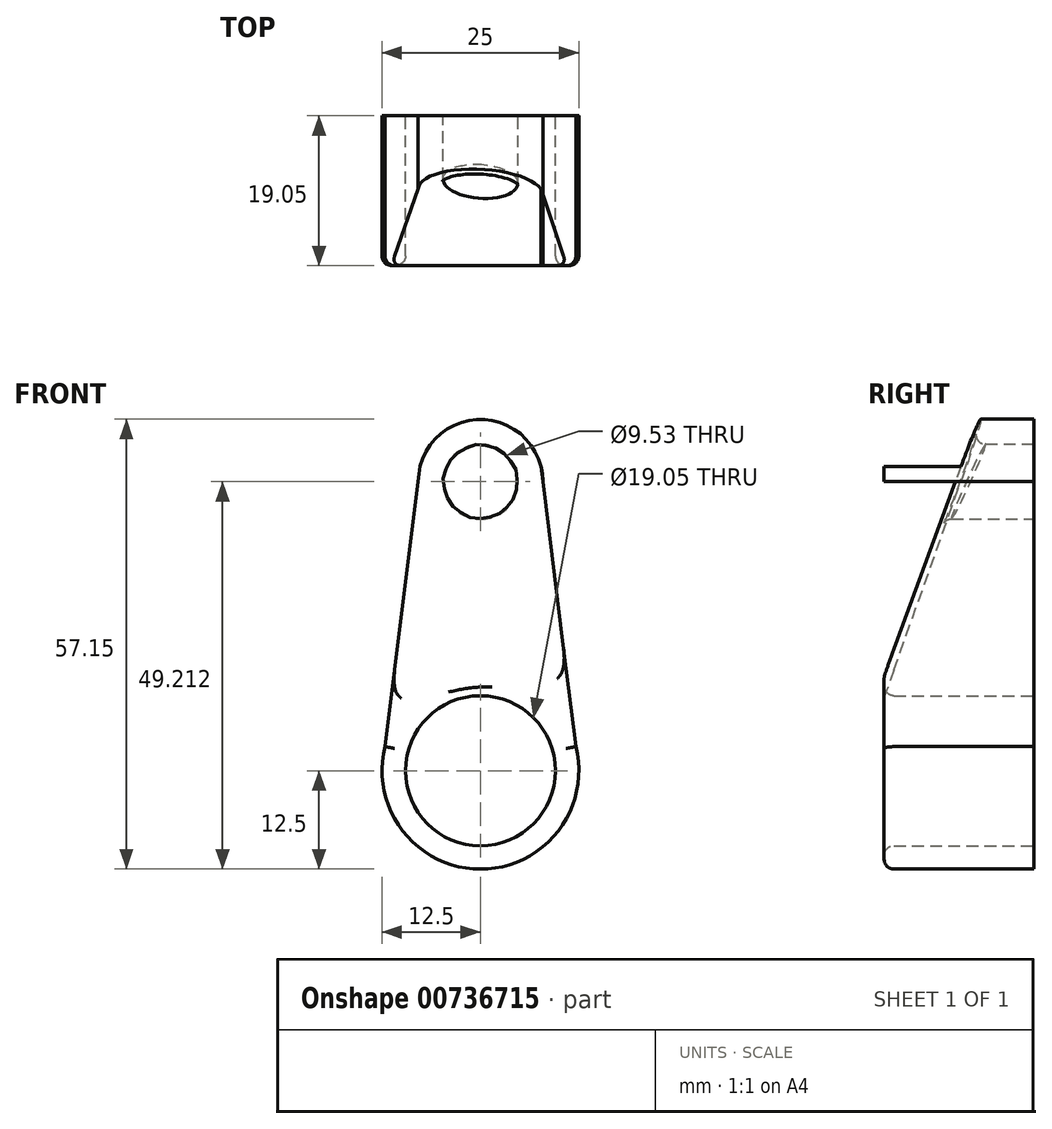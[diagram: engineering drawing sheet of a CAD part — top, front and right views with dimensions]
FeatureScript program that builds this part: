
annotation { "Feature Type Name" : "Feature", "Feature Type Description" : "" }
export const myFeature = defineFeature(function(context is Context, id is Id, definition is map)
    precondition{}
    {
        {
            var Q0;
            Q0=qCreatedBy(makeId("Front.planeOp"),FACE);
            var sketch = newSketch(context, id + "F0", { "sketchPlane" : qUnion([Q0])});
            skCircle(sketch, "E0", {"center": v(0, 0) * mm, "radius": 9.53 * mm});
            skCircle(sketch, "E1", {"center": v(0, 0) * mm, "radius": 12.5 * mm});
            skCircle(sketch, "E2", {"center": v(0, 36.71) * mm, "radius": 4.76 * mm});
            skCircle(sketch, "E3", {"center": v(0, 36.71) * mm, "radius": 7.94 * mm});
            skLineSegment(sketch, "E4", {"start": v(-12.5, 0) * mm, "end": v(-7.94, 36.71) * mm});
            skLineSegment(sketch, "E5", {"start": v(12.5, 0) * mm, "end": v(7.94, 36.71) * mm});
            skSolve(sketch);
        }
        {
            var Q0;
            Q0 = qSketchRegion(id + "F0", true);
            extrude(context, id + "F1", {"entities" : qUnion([Q0]), "depth" : 19.05 * mm, "offsetDistance" : 25 * mm});
        }
        {
            var Q0;
            Q0=makeQuery(id+"F1.opExtrude","SWEPT_FACE",FACE,{"disambiguationData":[OSD([sQuery(id+"F0.wireOp",EDGE,"E5")])]});
            var sketch = newSketch(context, id + "F2", { "sketchPlane" : qUnion([Q0])});
            skLineSegment(sketch, "E6", {"start": v(0, -1.87) * mm, "end": v(-19.05, -1.87) * mm, "construction": true});
            skLineSegment(sketch, "E7", {"start": v(-19.05, 10.63) * mm, "end": v(-19.05, 62.97) * mm});
            skLineSegment(sketch, "E8", {"start": v(-19.05, 62.97) * mm, "end": v(0, 62.97) * mm});
            skLineSegment(sketch, "E9", {"start": v(0, 62.97) * mm, "end": v(-19.05, 10.63) * mm});
            skSolve(sketch);
        }
        {
            var Q0;
            Q0 = qSketchRegion(id + "F2", true);
            extrude(context, id + "F3", {"entities" : qUnion([Q0]), "operationType" : NewBodyOperationType.REMOVE, "oppositeDirection" : true, "depth" : 25 * mm, "offsetDistance" : 25 * mm});
        }
        {
            var Q0;
            Q0=makeQuery(id+"F3.boolean.opBoolean","COPY",EDGE,{"derivedFrom":makeQuery(id+"F3.opExtrude","SWEPT_EDGE",EDGE,{"disambiguationData":[OSD([sQuery(id+"F0.wireOp",EDGE,"E5"),sQuery(id+"F2.wireOp",EDGE,"E7"),sQuery(id+"F2.wireOp",EDGE,"E9")])]})});
            var Q1;
            {var subQ0=sQuery(id+"F0.wireOp",EDGE,"E5");var subQ1=sQuery(id+"F0.wireOp",EDGE,"E4");var subQ2=sQuery(id+"F0.wireOp",EDGE,"E1");var subQ3=sQuery(id+"F0.wireOp",EDGE,"E0");Q1=makeQuery(id+"F3.boolean.opBoolean","SPLIT",FACE,{"disambiguationData":[TD([makeQuery(id+"F1.opExtrude","SWEPT_FACE",FACE,{"disambiguationData":[OSD([subQ3])]})])],"derivedFrom":makeQuery(id+"F1.opExtrude","CAP_FACE",FACE,{"disambiguationData":[OSD([subQ3,subQ2,sQuery(id+"F0.wireOp",EDGE,"E2"),sQuery(id+"F0.wireOp",EDGE,"E3"),subQ1,subQ0])],"isStart":false})});}
            fillet(context, id + "F4", {"entities" : qUnion([Q0, Q1]), "radius" : 1.25 * mm, "tangentPropagation" : true, "allowEdgeOverflow" : false});
        }
        {
            var Q0;
            Q0=makeQuery(id+"F3.boolean.opBoolean","INTERSECT",EDGE,{"derivedFrom":[makeQuery(id+"F1.opExtrude","SWEPT_FACE",FACE,{"disambiguationData":[OSD([sQuery(id+"F0.wireOp",EDGE,"E2")])]}),makeQuery(id+"F3.opExtrude","SWEPT_FACE",FACE,{"disambiguationData":[OSD([sQuery(id+"F2.wireOp",EDGE,"E9")])]})]});
            fillet(context, id + "F5", {"entities" : qUnion([Q0]), "radius" : 1.25 * mm, "tangentPropagation" : true, "allowEdgeOverflow" : false});
        }
    });
